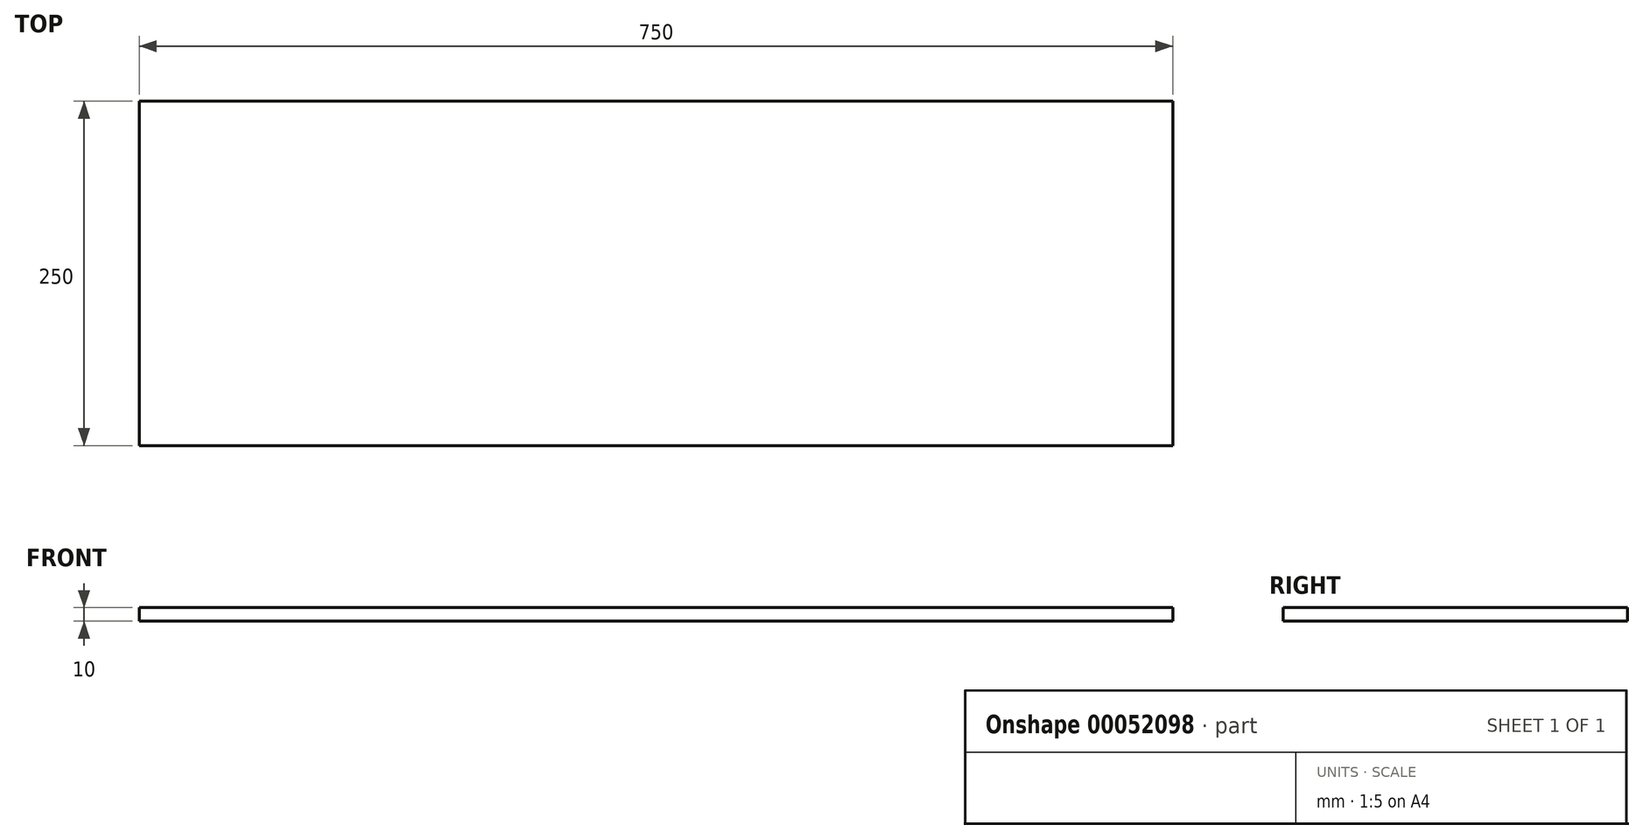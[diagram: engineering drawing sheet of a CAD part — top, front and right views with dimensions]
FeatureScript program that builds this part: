
annotation { "Feature Type Name" : "Feature", "Feature Type Description" : "" }
export const myFeature = defineFeature(function(context is Context, id is Id, definition is map)
    precondition{}
    {
        {
            var Q0;
            Q0=qCreatedBy(makeId("Top.planeOp"),FACE);
            var sketch = newSketch(context, id + "F0", { "sketchPlane" : qUnion([Q0])});
            skLineSegment(sketch, "E0.bottom", {"start": v(0, 0) * mm, "end": v(750, 0) * mm});
            skLineSegment(sketch, "E0.top", {"start": v(0, 250) * mm, "end": v(750, 250) * mm});
            skLineSegment(sketch, "E0.left", {"start": v(0, 0) * mm, "end": v(0, 250) * mm});
            skLineSegment(sketch, "E0.right", {"start": v(750, 0) * mm, "end": v(750, 250) * mm});
            skSolve(sketch);
        }
        {
            var Q0;
            Q0=makeQuery(id+"F0.imprint","IMPRINT",FACE,{"disambiguationData":[TD([[makeQuery(id+"F0.imprint","IMPRINT",EDGE,{"derivedFrom":sQuery(id+"F0.wireOp",EDGE,"E0.bottom")}),1.0]])]});
            extrude(context, id + "F1", {"entities" : qUnion([Q0]), "depth" : 10 * mm});
        }
    });
